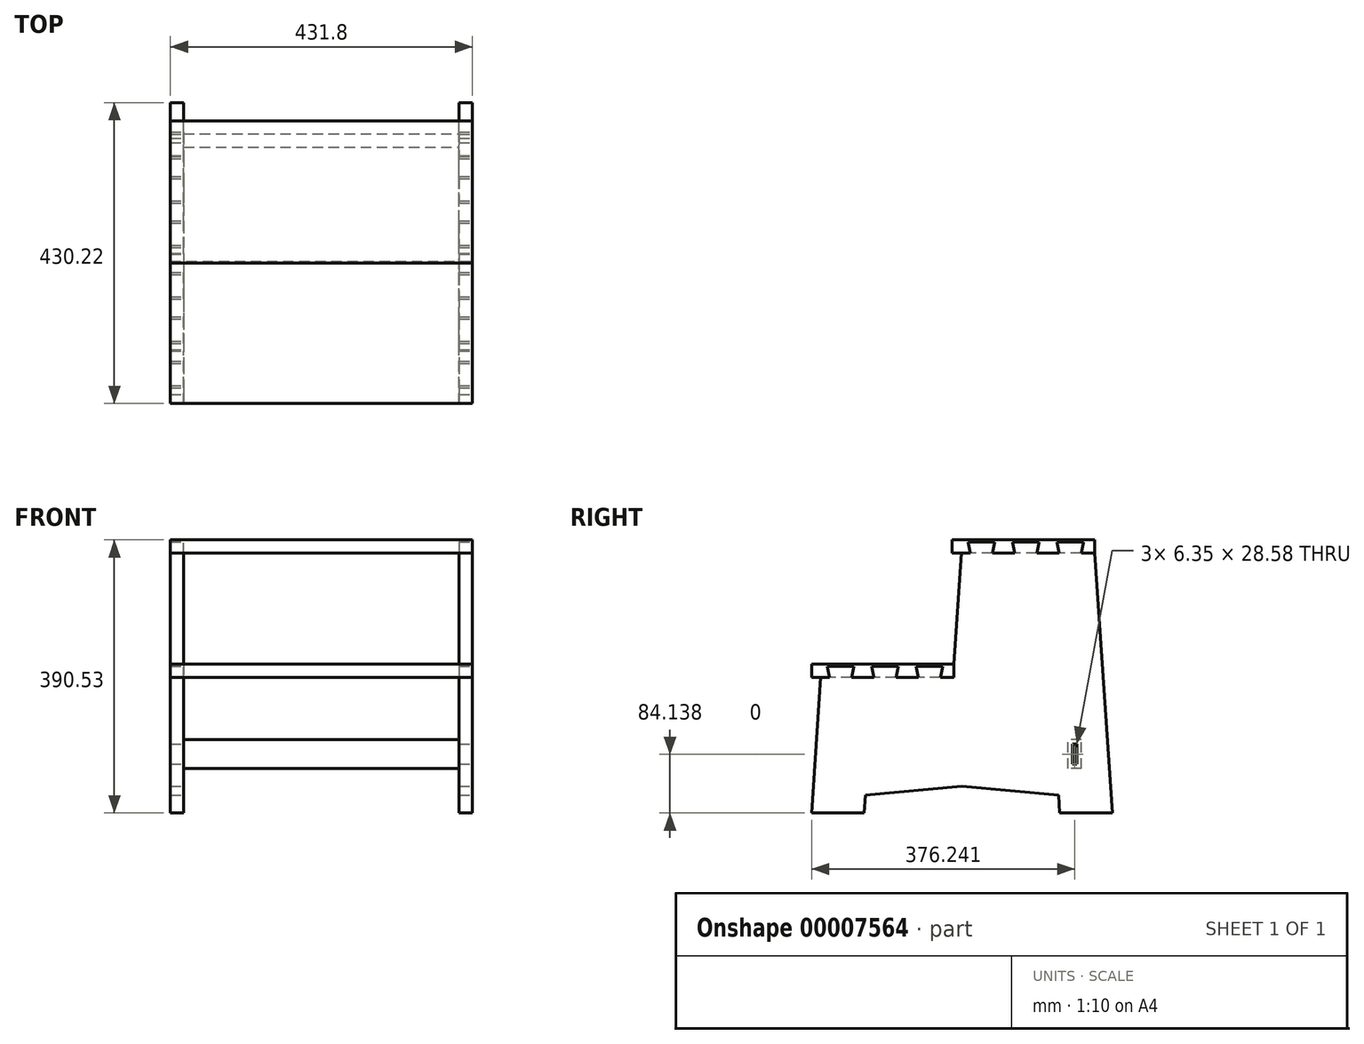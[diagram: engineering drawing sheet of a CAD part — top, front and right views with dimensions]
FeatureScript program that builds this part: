
annotation { "Feature Type Name" : "Feature", "Feature Type Description" : "" }
export const myFeature = defineFeature(function(context is Context, id is Id, definition is map)
    precondition{}
    {
        {
            var Q0;
            Q0=qCreatedBy(makeId("Right.planeOp"),FACE);
            var sketch = newSketch(context, id + "F0", { "sketchPlane" : qUnion([Q0])});
            skLineSegment(sketch, "E0", {"start": v(-215.1, 0) * mm, "end": v(215.1, 0) * mm});
            skLineSegment(sketch, "E1", {"start": v(215.1, 0) * mm, "end": v(189.24, 371.48) * mm});
            skLineSegment(sketch, "E2", {"start": v(-1.26, 371.48) * mm, "end": v(-11.78, 212.72) * mm});
            skLineSegment(sketch, "E3", {"start": v(-202.28, 193.68) * mm, "end": v(-215.1, 0) * mm});
            skLineSegment(sketch, "E4", {"start": v(-11.78, 193.67) * mm, "end": v(-202.28, 193.67) * mm});
            skLineSegment(sketch, "E5", {"start": v(-1.26, 371.48) * mm, "end": v(189.24, 371.48) * mm});
            skLineSegment(sketch, "E6", {"start": v(252.15, 0) * mm, "end": v(252.15, 371.48) * mm, "construction": true});
            skLineSegment(sketch, "E7", {"start": v(-342.78, 0) * mm, "end": v(-342.78, 193.67) * mm, "construction": true});
            skLineSegment(sketch, "E8", {"start": v(-11.78, 212.72) * mm, "end": v(-11.78, 193.67) * mm});
            skSolve(sketch);
        }
        {
            var Q0;
            Q0=makeQuery(id+"F0.imprint","IMPRINT",FACE,{"disambiguationData":[TD([[makeQuery(id+"F0.imprint","IMPRINT",EDGE,{"derivedFrom":sQuery(id+"F0.wireOp",EDGE,"E0")}),1.0]])]});
            var sketch = newSketch(context, id + "F1", { "sketchPlane" : qUnion([Q0])});
            skLineSegment(sketch, "E9.bottom", {"start": v(-214.98, 212.72) * mm, "end": v(-11.78, 212.72) * mm});
            skLineSegment(sketch, "E9.top", {"start": v(-214.98, 193.67) * mm, "end": v(-11.78, 193.67) * mm});
            skLineSegment(sketch, "E9.left", {"start": v(-214.98, 212.72) * mm, "end": v(-214.98, 193.67) * mm});
            skLineSegment(sketch, "E9.right", {"start": v(-11.78, 212.72) * mm, "end": v(-11.78, 193.67) * mm});
            skSolve(sketch);
        }
        {
            var Q0;
            Q0=makeQuery(id+"F0.imprint","IMPRINT",FACE,{"disambiguationData":[TD([[makeQuery(id+"F0.imprint","IMPRINT",EDGE,{"derivedFrom":sQuery(id+"F0.wireOp",EDGE,"E0")}),1.0]])]});
            var sketch = newSketch(context, id + "F2", { "sketchPlane" : qUnion([Q0])});
            skLineSegment(sketch, "E10.bottom", {"start": v(189.24, 371.48) * mm, "end": v(-13.96, 371.48) * mm});
            skLineSegment(sketch, "E10.top", {"start": v(189.24, 390.53) * mm, "end": v(-13.96, 390.53) * mm});
            skLineSegment(sketch, "E10.left", {"start": v(189.24, 371.48) * mm, "end": v(189.24, 390.53) * mm});
            skLineSegment(sketch, "E10.right", {"start": v(-13.96, 371.48) * mm, "end": v(-13.96, 390.53) * mm});
            skSolve(sketch);
        }
        {
            var Q0;
            Q0=makeQuery(id+"F0.imprint","IMPRINT",FACE,{"disambiguationData":[TD([[makeQuery(id+"F0.imprint","IMPRINT",EDGE,{"derivedFrom":sQuery(id+"F0.wireOp",EDGE,"E0")}),1.0]])]});
            var sketch = newSketch(context, id + "F3", { "sketchPlane" : qUnion([Q0])});
            skLineSegment(sketch, "E11", {"start": v(-139.7, 0) * mm, "end": v(139.7, 0) * mm});
            skLineSegment(sketch, "E12", {"start": v(139.7, 0) * mm, "end": v(137.94, 25.34) * mm});
            skLineSegment(sketch, "E13", {"start": v(137.94, 25.34) * mm, "end": v(0, 38.1) * mm});
            skLineSegment(sketch, "E14", {"start": v(0, 38.1) * mm, "end": v(-138.02, 25.34) * mm});
            skLineSegment(sketch, "E15", {"start": v(-138.02, 25.34) * mm, "end": v(-139.7, 0) * mm});
            skLineSegment(sketch, "E16", {"start": v(0, 38.1) * mm, "end": v(0, 0) * mm, "construction": true});
            skSolve(sketch);
        }
        {
            var Q0;
            Q0=makeQuery(id+"F0.imprint","IMPRINT",FACE,{"disambiguationData":[TD([[makeQuery(id+"F0.imprint","IMPRINT",EDGE,{"derivedFrom":sQuery(id+"F0.wireOp",EDGE,"E0")}),1.0]])]});
            var sketch = newSketch(context, id + "F4", { "sketchPlane" : qUnion([Q0])});
            skLineSegment(sketch, "E17.bottom", {"start": v(157.96, 98.43) * mm, "end": v(164.3, 98.43) * mm});
            skLineSegment(sketch, "E17.top", {"start": v(157.96, 69.85) * mm, "end": v(164.3, 69.85) * mm});
            skLineSegment(sketch, "E17.left", {"start": v(157.96, 98.43) * mm, "end": v(157.96, 69.85) * mm});
            skLineSegment(sketch, "E17.right", {"start": v(164.3, 98.43) * mm, "end": v(164.3, 69.85) * mm});
            skLineSegment(sketch, "E18", {"start": v(185.69, 0) * mm, "end": v(185.69, 69.85) * mm, "construction": true});
            skLineSegment(sketch, "E19", {"start": v(164.3, 0) * mm, "end": v(215.1, 0) * mm, "construction": true});
            skPoint(sketch, "E20", {"position": v(161.13, 98.43) * mm});
            skPoint(sketch, "E21", {"position": v(164.3, 84.14) * mm});
            skSolve(sketch);
        }
        {
            var Q0;
            {var subQ1=sQuery(id+"F1.wireOp",EDGE,"E9.right");Q0=makeQuery(id+"F1.imprint","IMPRINT",FACE,{"disambiguationData":[TD([[makeQuery(id+"F1.imprint","IMPRINT",EDGE,{"derivedFrom":subQ1}),1.0]])]});}
            var sketch = newSketch(context, id + "F5", { "sketchPlane" : qUnion([Q0])});
            skLineSegment(sketch, "E22.bottom", {"start": v(151.6, 104.78) * mm, "end": v(170.66, 104.78) * mm});
            skLineSegment(sketch, "E22.top", {"start": v(151.6, 63.5) * mm, "end": v(170.66, 63.5) * mm});
            skLineSegment(sketch, "E22.left", {"start": v(151.6, 104.78) * mm, "end": v(151.6, 63.5) * mm});
            skLineSegment(sketch, "E22.right", {"start": v(170.66, 104.78) * mm, "end": v(170.66, 63.5) * mm});
            skPoint(sketch, "E23", {"position": v(161.13, 104.78) * mm});
            skPoint(sketch, "E24", {"position": v(170.66, 84.14) * mm});
            skSolve(sketch);
        }
        {
            var Q0;
            Q0=makeQuery(id+"F1.imprint","IMPRINT",FACE,{"disambiguationData":[TD([[makeQuery(id+"F1.imprint","IMPRINT",EDGE,{"derivedFrom":sQuery(id+"F1.wireOp",EDGE,"E9.bottom")}),-1.0]])]});
            var sketch = newSketch(context, id + "F6", { "sketchPlane" : qUnion([Q0])});
            skLineSegment(sketch, "E25", {"start": v(-189.58, 193.67) * mm, "end": v(-192.75, 209.55) * mm});
            skLineSegment(sketch, "E26", {"start": v(-192.75, 209.55) * mm, "end": v(-154.65, 209.55) * mm});
            skLineSegment(sketch, "E27", {"start": v(-154.65, 209.55) * mm, "end": v(-157.83, 193.67) * mm});
            skLineSegment(sketch, "E28", {"start": v(-126.08, 193.67) * mm, "end": v(-129.25, 209.55) * mm});
            skLineSegment(sketch, "E29", {"start": v(-129.25, 209.55) * mm, "end": v(-91.15, 209.55) * mm});
            skLineSegment(sketch, "E30", {"start": v(-91.15, 209.55) * mm, "end": v(-94.33, 193.67) * mm});
            skLineSegment(sketch, "E31", {"start": v(-62.58, 193.67) * mm, "end": v(-65.75, 209.55) * mm});
            skLineSegment(sketch, "E32", {"start": v(-65.75, 209.55) * mm, "end": v(-27.65, 209.55) * mm});
            skLineSegment(sketch, "E33", {"start": v(-27.65, 209.55) * mm, "end": v(-30.83, 193.67) * mm});
            skLineSegment(sketch, "E34", {"start": v(-30.83, 193.67) * mm, "end": v(-62.58, 193.67) * mm});
            skLineSegment(sketch, "E35", {"start": v(-189.58, 193.67) * mm, "end": v(-157.83, 193.67) * mm});
            skLineSegment(sketch, "E36", {"start": v(-126.08, 193.67) * mm, "end": v(-94.33, 193.67) * mm});
            skLineSegment(sketch, "E37", {"start": v(-189.58, 193.67) * mm, "end": v(-202.28, 193.67) * mm, "construction": true});
            skLineSegment(sketch, "E38", {"start": v(-157.83, 193.67) * mm, "end": v(-126.08, 193.67) * mm, "construction": true});
            skLineSegment(sketch, "E39", {"start": v(-94.33, 193.67) * mm, "end": v(-62.58, 193.67) * mm, "construction": true});
            skLineSegment(sketch, "E40", {"start": v(-62.58, 193.67) * mm, "end": v(-30.83, 193.67) * mm});
            skLineSegment(sketch, "E41", {"start": v(-30.83, 193.67) * mm, "end": v(-11.78, 193.67) * mm, "construction": true});
            skLineSegment(sketch, "E42", {"start": v(-214.98, 212.72) * mm, "end": v(-214.98, 209.55) * mm, "construction": true});
            skPoint(sketch, "E43", {"position": v(-173.7, 209.55) * mm});
            skPoint(sketch, "E44", {"position": v(-110.2, 209.55) * mm});
            skPoint(sketch, "E45", {"position": v(-46.7, 209.55) * mm});
            skPoint(sketch, "E46", {"position": v(-46.7, 193.67) * mm});
            skPoint(sketch, "E47", {"position": v(-110.2, 193.67) * mm});
            skPoint(sketch, "E48", {"position": v(-173.7, 193.67) * mm});
            skSolve(sketch);
        }
        {
            var Q0;
            Q0=makeQuery(id+"F0.imprint","IMPRINT",FACE,{"disambiguationData":[TD([[makeQuery(id+"F0.imprint","IMPRINT",EDGE,{"derivedFrom":sQuery(id+"F0.wireOp",EDGE,"E0")}),1.0]])]});
            extrude(context, id + "F7", {"entities" : qUnion([Q0]), "oppositeDirection" : true, "depth" : 19.05 * mm});
        }
        {
            var Q0;
            Q0 = qSketchRegion(id + "F6", true);
            extrude(context, id + "F8", {"entities" : qUnion([Q0]), "oppositeDirection" : true, "depth" : 19.05 * mm});
        }
        {
            var Q0;
            Q0=makeQuery(id+"F4.imprint","IMPRINT",FACE,{"disambiguationData":[TD([[makeQuery(id+"F4.imprint","IMPRINT",EDGE,{"derivedFrom":sQuery(id+"F4.wireOp",EDGE,"E17.bottom")}),1.0]])]});
            var sketch = newSketch(context, id + "F9", { "sketchPlane" : qUnion([Q0])});
            skLineSegment(sketch, "E49", {"start": v(-11.78, 193.67) * mm, "end": v(189.24, 371.48) * mm, "construction": true});
            skSolve(sketch);
        }
        {
            var Q0;
            Q0=makeQuery(id+"F8.opExtrude","SWEPT_BODY",BODY,{"disambiguationData":[OSD([sQuery(id+"F6.wireOp",EDGE,"E25"),sQuery(id+"F6.wireOp",EDGE,"E26"),sQuery(id+"F6.wireOp",EDGE,"E27"),sQuery(id+"F6.wireOp",EDGE,"E35")])]});
            var Q1;
            Q1=makeQuery(id+"F8.opExtrude","SWEPT_BODY",BODY,{"disambiguationData":[OSD([sQuery(id+"F6.wireOp",EDGE,"E28"),sQuery(id+"F6.wireOp",EDGE,"E29"),sQuery(id+"F6.wireOp",EDGE,"E30"),sQuery(id+"F6.wireOp",EDGE,"E36")])]});
            var Q2;
            Q2=makeQuery(id+"F8.opExtrude","SWEPT_BODY",BODY,{"disambiguationData":[OSD([sQuery(id+"F6.wireOp",EDGE,"E31"),sQuery(id+"F6.wireOp",EDGE,"E32"),sQuery(id+"F6.wireOp",EDGE,"E33"),sQuery(id+"F6.wireOp",EDGE,"E40")])]});
            var Q3;
            Q3=sQuery(id+"F9.wireOp",EDGE,"E49");
            transform(context, id + "F10", {"entities" : qUnion([Q0, Q1, Q2]), "transformType" : TransformType.TRANSLATION_ENTITY, "oppositeDirectionEntity" : false, "transformLine" : qUnion([Q3]), "makeCopy" : true});
        }
        {
            var Q0;
            Q0=makeQuery(id+"F10.opPattern","COPY",BODY,{"derivedFrom":makeQuery(id+"F8.opExtrude","SWEPT_BODY",BODY,{"disambiguationData":[OSD([sQuery(id+"F6.wireOp",EDGE,"E25"),sQuery(id+"F6.wireOp",EDGE,"E26"),sQuery(id+"F6.wireOp",EDGE,"E27"),sQuery(id+"F6.wireOp",EDGE,"E35")])]}),"instanceName":"1"});
            var Q1;
            Q1=makeQuery(id+"F10.opPattern","COPY",BODY,{"derivedFrom":makeQuery(id+"F8.opExtrude","SWEPT_BODY",BODY,{"disambiguationData":[OSD([sQuery(id+"F6.wireOp",EDGE,"E28"),sQuery(id+"F6.wireOp",EDGE,"E29"),sQuery(id+"F6.wireOp",EDGE,"E30"),sQuery(id+"F6.wireOp",EDGE,"E36")])]}),"instanceName":"1"});
            var Q2;
            Q2=makeQuery(id+"F10.opPattern","COPY",BODY,{"derivedFrom":makeQuery(id+"F8.opExtrude","SWEPT_BODY",BODY,{"disambiguationData":[OSD([sQuery(id+"F6.wireOp",EDGE,"E31"),sQuery(id+"F6.wireOp",EDGE,"E32"),sQuery(id+"F6.wireOp",EDGE,"E33"),sQuery(id+"F6.wireOp",EDGE,"E40")])]}),"instanceName":"1"});
            var Q3;
            Q3=makeQuery(id+"F8.opExtrude","SWEPT_BODY",BODY,{"disambiguationData":[OSD([sQuery(id+"F6.wireOp",EDGE,"E31"),sQuery(id+"F6.wireOp",EDGE,"E32"),sQuery(id+"F6.wireOp",EDGE,"E33"),sQuery(id+"F6.wireOp",EDGE,"E40")])]});
            var Q4;
            Q4=makeQuery(id+"F7.opExtrude","SWEPT_BODY",BODY,{"disambiguationData":[OSD([sQuery(id+"F0.wireOp",EDGE,"E0"),sQuery(id+"F0.wireOp",EDGE,"E1"),sQuery(id+"F0.wireOp",EDGE,"E2"),sQuery(id+"F0.wireOp",EDGE,"E3"),sQuery(id+"F0.wireOp",EDGE,"E4"),sQuery(id+"F0.wireOp",EDGE,"E5"),sQuery(id+"F0.wireOp",EDGE,"E8")])]});
            var Q5;
            Q5=makeQuery(id+"F8.opExtrude","SWEPT_BODY",BODY,{"disambiguationData":[OSD([sQuery(id+"F6.wireOp",EDGE,"E25"),sQuery(id+"F6.wireOp",EDGE,"E26"),sQuery(id+"F6.wireOp",EDGE,"E27"),sQuery(id+"F6.wireOp",EDGE,"E35")])]});
            var Q6;
            Q6=makeQuery(id+"F8.opExtrude","SWEPT_BODY",BODY,{"disambiguationData":[OSD([sQuery(id+"F6.wireOp",EDGE,"E28"),sQuery(id+"F6.wireOp",EDGE,"E29"),sQuery(id+"F6.wireOp",EDGE,"E30"),sQuery(id+"F6.wireOp",EDGE,"E36")])]});
            booleanBodies(context, id + "F11", {"operationType" : BooleanOperationType.UNION, "tools" : qUnion([Q0, Q1, Q2, Q3, Q4, Q5, Q6])});
        }
        {
            var Q0;
            Q0 = qSketchRegion(id + "F1", true);
            extrude(context, id + "F12", {"entities" : qUnion([Q0]), "oppositeDirection" : true, "depth" : 431.8 * mm});
        }
        {
            var Q0;
            Q0 = qSketchRegion(id + "F2", true);
            extrude(context, id + "F13", {"entities" : qUnion([Q0]), "oppositeDirection" : true, "depth" : 431.8 * mm});
        }
        {
            var Q0;
            Q0 = qSketchRegion(id + "F3", true);
            extrude(context, id + "F14", {"entities" : qUnion([Q0]), "operationType" : NewBodyOperationType.REMOVE, "endBound" : BoundingType.UP_TO_NEXT, "oppositeDirection" : true, "depth" : 25.4 * mm});
        }
        {
            var Q0;
            Q0 = qSketchRegion(id + "F4", true);
            extrude(context, id + "F15", {"entities" : qUnion([Q0]), "operationType" : NewBodyOperationType.REMOVE, "endBound" : BoundingType.UP_TO_NEXT, "oppositeDirection" : true, "depth" : 25.4 * mm});
        }
        {
            var Q0;
            Q0=makeQuery(id+"F13.opExtrude","SWEPT_FACE",FACE,{"disambiguationData":[OSD([sQuery(id+"F2.wireOp",EDGE,"E10.bottom")])]});
            var sketch = newSketch(context, id + "F16", { "sketchPlane" : qUnion([Q0])});
            skLineSegment(sketch, "E50", {"start": v(-19.05, 1.26) * mm, "end": v(-431.8, 1.26) * mm, "construction": true});
            skSolve(sketch);
        }
        {
            var Q0;
            Q0=makeQuery(id+"F10.opPattern","COPY",BODY,{"derivedFrom":makeQuery(id+"F8.opExtrude","SWEPT_BODY",BODY,{"disambiguationData":[OSD([sQuery(id+"F6.wireOp",EDGE,"E25"),sQuery(id+"F6.wireOp",EDGE,"E26"),sQuery(id+"F6.wireOp",EDGE,"E27"),sQuery(id+"F6.wireOp",EDGE,"E35")])]}),"instanceName":"1"});
            var Q1;
            Q1=sQuery(id+"F16.wireOp",EDGE,"E50");
            transform(context, id + "F17", {"entities" : qUnion([Q0]), "transformType" : TransformType.TRANSLATION_ENTITY, "oppositeDirectionEntity" : false, "transformLine" : qUnion([Q1]), "makeCopy" : true});
        }
        {
            var Q0;
            Q0=makeQuery(id+"F10.opPattern","COPY",BODY,{"derivedFrom":makeQuery(id+"F8.opExtrude","SWEPT_BODY",BODY,{"disambiguationData":[OSD([sQuery(id+"F6.wireOp",EDGE,"E25"),sQuery(id+"F6.wireOp",EDGE,"E26"),sQuery(id+"F6.wireOp",EDGE,"E27"),sQuery(id+"F6.wireOp",EDGE,"E35")])]}),"instanceName":"1"});
            var Q1;
            Q1=makeQuery(id+"F17.opPattern","COPY",BODY,{"derivedFrom":makeQuery(id+"F10.opPattern","COPY",BODY,{"derivedFrom":makeQuery(id+"F8.opExtrude","SWEPT_BODY",BODY,{"disambiguationData":[OSD([sQuery(id+"F6.wireOp",EDGE,"E25"),sQuery(id+"F6.wireOp",EDGE,"E26"),sQuery(id+"F6.wireOp",EDGE,"E27"),sQuery(id+"F6.wireOp",EDGE,"E35")])]}),"instanceName":"1"}),"instanceName":"1"});
            var Q2;
            Q2=makeQuery(id+"F12.opExtrude","SWEPT_BODY",BODY,{"disambiguationData":[OSD([sQuery(id+"F1.wireOp",EDGE,"E9.bottom"),sQuery(id+"F1.wireOp",EDGE,"E9.top"),sQuery(id+"F1.wireOp",EDGE,"E9.left"),sQuery(id+"F1.wireOp",EDGE,"E9.right")])]});
            var Q3;
            Q3=makeQuery(id+"F13.opExtrude","SWEPT_BODY",BODY,{"disambiguationData":[OSD([sQuery(id+"F2.wireOp",EDGE,"E10.bottom"),sQuery(id+"F2.wireOp",EDGE,"E10.top"),sQuery(id+"F2.wireOp",EDGE,"E10.left"),sQuery(id+"F2.wireOp",EDGE,"E10.right")])]});
            booleanBodies(context, id + "F18", {"operationType" : BooleanOperationType.SUBTRACTION, "tools" : qUnion([Q0, Q1]), "targets" : qUnion([Q2, Q3]), "keepTools" : true});
        }
        {
            var Q0;
            Q0 = qSketchRegion(id + "F5", true);
            var Q1;
            {var subQ0=makeQuery(id+"F8.opExtrude","CAP_FACE",FACE,{"disambiguationData":[OSD([sQuery(id+"F6.wireOp",EDGE,"E25"),sQuery(id+"F6.wireOp",EDGE,"E26"),sQuery(id+"F6.wireOp",EDGE,"E27"),sQuery(id+"F6.wireOp",EDGE,"E35")])],"isStart":false});var subQ1=makeQuery(id+"F8.opExtrude","CAP_FACE",FACE,{"disambiguationData":[OSD([sQuery(id+"F6.wireOp",EDGE,"E28"),sQuery(id+"F6.wireOp",EDGE,"E29"),sQuery(id+"F6.wireOp",EDGE,"E30"),sQuery(id+"F6.wireOp",EDGE,"E36")])],"isStart":false});var subQ2=makeQuery(id+"F8.opExtrude","CAP_FACE",FACE,{"disambiguationData":[OSD([sQuery(id+"F6.wireOp",EDGE,"E31"),sQuery(id+"F6.wireOp",EDGE,"E32"),sQuery(id+"F6.wireOp",EDGE,"E33"),sQuery(id+"F6.wireOp",EDGE,"E40")])],"isStart":false});Q1=makeQuery(id+"F17.opPattern","COPY",FACE,{"derivedFrom":makeQuery(id+"F11.opBoolean","MERGE",FACE,{"derivedFrom":[makeQuery(id+"F7.opExtrude","CAP_FACE",FACE,{"disambiguationData":[OSD([sQuery(id+"F0.wireOp",EDGE,"E0"),sQuery(id+"F0.wireOp",EDGE,"E1"),sQuery(id+"F0.wireOp",EDGE,"E2"),sQuery(id+"F0.wireOp",EDGE,"E3"),sQuery(id+"F0.wireOp",EDGE,"E4"),sQuery(id+"F0.wireOp",EDGE,"E5"),sQuery(id+"F0.wireOp",EDGE,"E8")])],"isStart":false}),subQ0,subQ1,subQ2,makeQuery(id+"F10.opPattern","COPY",FACE,{"derivedFrom":subQ0,"instanceName":"1"}),makeQuery(id+"F10.opPattern","COPY",FACE,{"derivedFrom":subQ1,"instanceName":"1"}),makeQuery(id+"F10.opPattern","COPY",FACE,{"derivedFrom":subQ2,"instanceName":"1"})]}),"instanceName":"1"});}
            extrude(context, id + "F19", {"entities" : qUnion([Q0]), "endBound" : BoundingType.UP_TO_SURFACE, "oppositeDirection" : true, "endBoundEntityFace" : qUnion([Q1]), "depth" : 25.4 * mm});
        }
        {
            var Q0;
            Q0=makeQuery(id+"F10.opPattern","COPY",BODY,{"derivedFrom":makeQuery(id+"F8.opExtrude","SWEPT_BODY",BODY,{"disambiguationData":[OSD([sQuery(id+"F6.wireOp",EDGE,"E25"),sQuery(id+"F6.wireOp",EDGE,"E26"),sQuery(id+"F6.wireOp",EDGE,"E27"),sQuery(id+"F6.wireOp",EDGE,"E35")])]}),"instanceName":"1"});
            var Q1;
            Q1=makeQuery(id+"F17.opPattern","COPY",BODY,{"derivedFrom":makeQuery(id+"F10.opPattern","COPY",BODY,{"derivedFrom":makeQuery(id+"F8.opExtrude","SWEPT_BODY",BODY,{"disambiguationData":[OSD([sQuery(id+"F6.wireOp",EDGE,"E25"),sQuery(id+"F6.wireOp",EDGE,"E26"),sQuery(id+"F6.wireOp",EDGE,"E27"),sQuery(id+"F6.wireOp",EDGE,"E35")])]}),"instanceName":"1"}),"instanceName":"1"});
            var Q2;
            Q2=makeQuery(id+"F19.opExtrude","SWEPT_BODY",BODY,{"disambiguationData":[OSD([sQuery(id+"F5.wireOp",EDGE,"E22.bottom"),sQuery(id+"F5.wireOp",EDGE,"E22.top"),sQuery(id+"F5.wireOp",EDGE,"E22.left"),sQuery(id+"F5.wireOp",EDGE,"E22.right")])]});
            booleanBodies(context, id + "F20", {"operationType" : BooleanOperationType.SUBTRACTION, "tools" : qUnion([Q0, Q1]), "targets" : qUnion([Q2]), "keepTools" : true});
        }
    });
